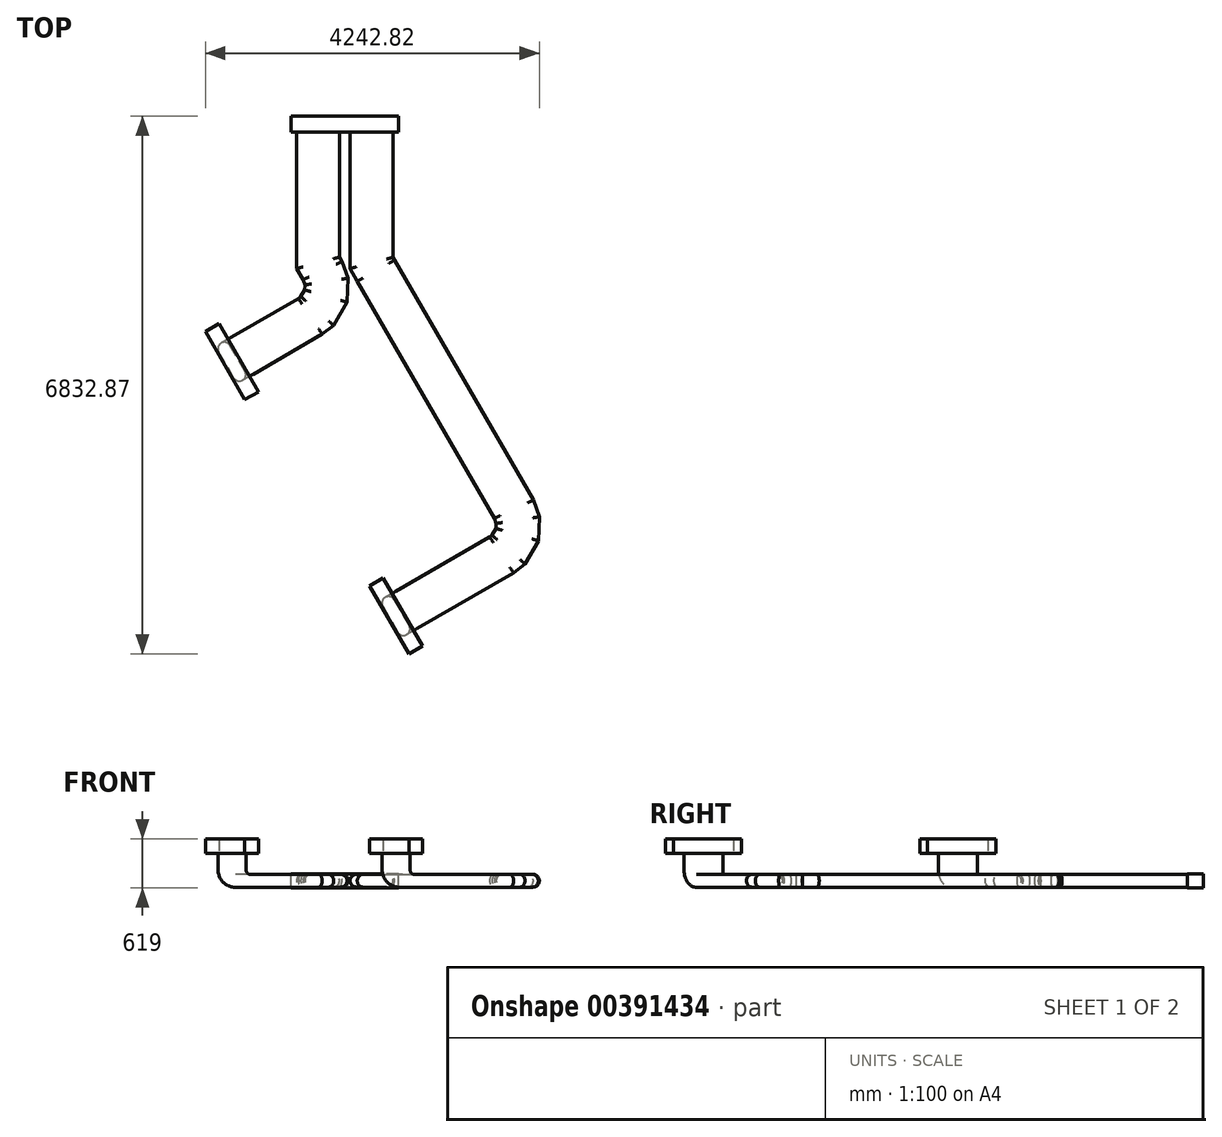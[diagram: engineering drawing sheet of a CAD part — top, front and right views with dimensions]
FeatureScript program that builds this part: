
annotation { "Feature Type Name" : "Feature", "Feature Type Description" : "" }
export const myFeature = defineFeature(function(context is Context, id is Id, definition is map)
    precondition{}
    {
        {
            var Q0;
            Q0=qCreatedBy(makeId("Front.planeOp"),FACE);
            var sketch = newSketch(context, id + "F0", { "sketchPlane" : qUnion([Q0])});
            skLineSegment(sketch, "E0.bottom", {"start": v(680, -89) * mm, "end": v(-680, -89) * mm});
            skLineSegment(sketch, "E0.top", {"start": v(680, 89) * mm, "end": v(-680, 89) * mm});
            skLineSegment(sketch, "E0.left", {"start": v(680, -89) * mm, "end": v(680, 89) * mm});
            skLineSegment(sketch, "E0.right", {"start": v(-680, -89) * mm, "end": v(-680, 89) * mm});
            skPoint(sketch, "E0.middle", {"position": v(0, 0) * mm});
            skSolve(sketch);
        }
        {
            var Q0;
            Q0=qSketchRegion(id+"F0",true);
            extrude(context, id + "F1", {"entities" : qUnion([Q0]), "depth" : 200 * mm});
        }
        {
            var Q0;
            Q0=makeQuery(id+"F1.opExtrude","CAP_FACE",FACE,{"disambiguationData":[OSD([sQuery(id+"F0.wireOp",EDGE,"E0.bottom"),sQuery(id+"F0.wireOp",EDGE,"E0.top"),sQuery(id+"F0.wireOp",EDGE,"E0.left"),sQuery(id+"F0.wireOp",EDGE,"E0.right")])],"isStart":false});
            var sketch = newSketch(context, id + "F2", { "sketchPlane" : qUnion([Q0])});
            skLineSegment(sketch, "E1.bottom", {"start": v(-150, -82.5) * mm, "end": v(-530, -82.5) * mm});
            skLineSegment(sketch, "E1.top", {"start": v(-150, 82.5) * mm, "end": v(-530, 82.5) * mm});
            skPoint(sketch, "E1.middle", {"position": v(-340, 0) * mm});
            skArc(sketch, "E2", {"start": v(-530, 82.5) * mm, "mid": v(-612.5, 0) * mm, "end": v(-530, -82.5) * mm});
            skArc(sketch, "E3", {"start": v(-150, -82.5) * mm, "mid": v(-67.5, 0) * mm, "end": v(-150, 82.5) * mm});
            skLineSegment(sketch, "E4.MirrorCS", {"start": v(150, -82.5) * mm, "end": v(530, -82.5) * mm});
            skLineSegment(sketch, "E5.MirrorCS", {"start": v(150, 82.5) * mm, "end": v(530, 82.5) * mm});
            skArc(sketch, "E6.MirrorCS", {"start": v(150, -82.5) * mm, "mid": v(67.5, 0) * mm, "end": v(150, 82.5) * mm});
            skArc(sketch, "E7.MirrorCS", {"start": v(530, 82.5) * mm, "mid": v(612.5, 0) * mm, "end": v(530, -82.5) * mm});
            skSolve(sketch);
        }
        {
            var Q0;
            Q0=makeQuery(id+"F2.imprint","IMPRINT",FACE,{"disambiguationData":[TD([[makeQuery(id+"F2.imprint","IMPRINT",EDGE,{"derivedFrom":sQuery(id+"F2.wireOp",EDGE,"E1.bottom")}),-1.0]])]});
            var Q1;
            Q1=makeQuery(id+"F2.imprint","IMPRINT",FACE,{"disambiguationData":[TD([[makeQuery(id+"F2.imprint","IMPRINT",EDGE,{"derivedFrom":sQuery(id+"F2.wireOp",EDGE,"E4.MirrorCS")}),1.0]])]});
            extrude(context, id + "F3", {"entities" : qUnion([Q0, Q1]), "operationType" : NewBodyOperationType.ADD, "depth" : 50 * mm});
        }
        {
            var Q0;
            Q0=makeQuery(id+"F1.opExtrude","SWEPT_BODY",BODY,{"disambiguationData":[OSD([sQuery(id+"F0.wireOp",EDGE,"E0.bottom"),sQuery(id+"F0.wireOp",EDGE,"E0.top"),sQuery(id+"F0.wireOp",EDGE,"E0.left"),sQuery(id+"F0.wireOp",EDGE,"E0.right")])]});
            transform(context, id + "F4", {"entities" : qUnion([Q0]), "transformType" : TransformType.TRANSLATION_3D, "dx" : 0 * mm, "dy" : 0 * mm, "dz" : 0 * mm, "makeCopy" : true});
        }
        {
            var Q0;
            Q0=makeQuery(id+"F4.opPattern","COPY",BODY,{"derivedFrom":makeQuery(id+"F1.opExtrude","SWEPT_BODY",BODY,{"disambiguationData":[OSD([sQuery(id+"F0.wireOp",EDGE,"E0.bottom"),sQuery(id+"F0.wireOp",EDGE,"E0.top"),sQuery(id+"F0.wireOp",EDGE,"E0.left"),sQuery(id+"F0.wireOp",EDGE,"E0.right")])]}),"instanceName":"1"});
            deleteBodies(context, id + "F5", {"entities" : qUnion([Q0])});
        }
        {
            var Q0;
            Q0=makeQuery(id+"F1.opExtrude","SWEPT_BODY",BODY,{"disambiguationData":[OSD([sQuery(id+"F0.wireOp",EDGE,"E0.bottom"),sQuery(id+"F0.wireOp",EDGE,"E0.top"),sQuery(id+"F0.wireOp",EDGE,"E0.left"),sQuery(id+"F0.wireOp",EDGE,"E0.right")])]});
            transform(context, id + "F6", {"entities" : qUnion([Q0]), "transformType" : TransformType.COPY});
        }
        {
            var Q0;
            Q0=makeQuery(id+"F6.opPattern","COPY",BODY,{"derivedFrom":makeQuery(id+"F1.opExtrude","SWEPT_BODY",BODY,{"disambiguationData":[OSD([sQuery(id+"F0.wireOp",EDGE,"E0.bottom"),sQuery(id+"F0.wireOp",EDGE,"E0.top"),sQuery(id+"F0.wireOp",EDGE,"E0.left"),sQuery(id+"F0.wireOp",EDGE,"E0.right")])]}),"instanceName":"1"});
            transform(context, id + "F7", {"entities" : qUnion([Q0]), "transformType" : TransformType.TRANSLATION_3D, "dx" : 0 * mm, "dy" : 0 * mm, "dz" : 0 * mm, "makeCopy" : true});
        }
        {
            var Q0;
            Q0=makeQuery(id+"F7.opPattern","COPY",BODY,{"derivedFrom":makeQuery(id+"F6.opPattern","COPY",BODY,{"derivedFrom":makeQuery(id+"F1.opExtrude","SWEPT_BODY",BODY,{"disambiguationData":[OSD([sQuery(id+"F0.wireOp",EDGE,"E0.bottom"),sQuery(id+"F0.wireOp",EDGE,"E0.top"),sQuery(id+"F0.wireOp",EDGE,"E0.left"),sQuery(id+"F0.wireOp",EDGE,"E0.right")])]}),"instanceName":"1"}),"instanceName":"1"});
            deleteBodies(context, id + "F8", {"entities" : qUnion([Q0])});
        }
        {
            var Q0;
            Q0=makeQuery(id+"F6.opPattern","COPY",BODY,{"derivedFrom":makeQuery(id+"F1.opExtrude","SWEPT_BODY",BODY,{"disambiguationData":[OSD([sQuery(id+"F0.wireOp",EDGE,"E0.bottom"),sQuery(id+"F0.wireOp",EDGE,"E0.top"),sQuery(id+"F0.wireOp",EDGE,"E0.left"),sQuery(id+"F0.wireOp",EDGE,"E0.right")])]}),"instanceName":"1"});
            deleteBodies(context, id + "F9", {"entities" : qUnion([Q0])});
        }
        {
            var Q0;
            Q0=makeQuery(id+"F3.opExtrude","CAP_FACE",FACE,{"disambiguationData":[OSD([sQuery(id+"F2.wireOp",EDGE,"E1.bottom"),sQuery(id+"F2.wireOp",EDGE,"E1.top"),sQuery(id+"F2.wireOp",EDGE,"E2"),sQuery(id+"F2.wireOp",EDGE,"E3")])],"isStart":false});
            var sketch = newSketch(context, id + "F10", { "sketchPlane" : qUnion([Q0])});
            skSolve(sketch);
        }
        {
            var Q0;
            Q0=makeQuery(id+"F10.imprint","IMPRINT",FACE,{"disambiguationData":[TD([[makeQuery(id+"F10.imprint","IMPRINT",EDGE,{"derivedFrom":makeQuery(id+"F3.opExtrude","CAP_EDGE",EDGE,{"disambiguationData":[OSD([sQuery(id+"F2.wireOp",EDGE,"E1.bottom")])],"isStart":false})}),-1.0]])]});
            var sketch = newSketch(context, id + "F11", { "sketchPlane" : qUnion([Q0])});
            skPoint(sketch, "E8.0", {"position": v(-340, 82.5) * mm});
            skPoint(sketch, "E8.1", {"position": v(-340, -82.5) * mm});
            skPoint(sketch, "E8.2", {"position": v(-612.5, 0) * mm});
            skPoint(sketch, "E8.3", {"position": v(-67.5, 0) * mm});
            skPoint(sketch, "E8.4", {"position": v(67.5, 0) * mm});
            skPoint(sketch, "E8.5", {"position": v(340, -82.5) * mm});
            skPoint(sketch, "E8.6", {"position": v(340, 82.5) * mm});
            skPoint(sketch, "E8.7", {"position": v(612.5, 0) * mm});
            skLineSegment(sketch, "E9", {"start": v(-612.5, 0) * mm, "end": v(612.5, 0) * mm, "construction": true});
            skLineSegment(sketch, "E10", {"start": v(-340, 82.5) * mm, "end": v(-340, -82.5) * mm, "construction": true});
            skLineSegment(sketch, "E11", {"start": v(340, 82.5) * mm, "end": v(340, -82.5) * mm, "construction": true});
            skPoint(sketch, "E12", {"position": v(-340, 0) * mm});
            skPoint(sketch, "E13", {"position": v(340, 0) * mm});
            skSolve(sketch);
        }
        {
            var Q0;
            Q0=qCreatedBy(makeId("Top.planeOp"),FACE);
            var sketch = newSketch(context, id + "F12", { "sketchPlane" : qUnion([Q0])});
            skPoint(sketch, "E14.0", {"position": v(340, -250) * mm});
            skPoint(sketch, "E14.1", {"position": v(-340, -250) * mm});
            skLineSegment(sketch, "E15", {"start": v(-340, -250) * mm, "end": v(-340, -1750) * mm});
            skLineSegment(sketch, "E16", {"start": v(340, -250) * mm, "end": v(340, -1750) * mm});
            skLineSegment(sketch, "E17", {"start": v(-283.06, -1962.5) * mm, "end": v(85, -1750) * mm, "construction": true});
            skLineSegment(sketch, "E18", {"start": v(395.32, -1963.44) * mm, "end": v(763.27, -1750.74) * mm, "construction": true});
            skLineSegment(sketch, "E19", {"start": v(-340, -1750) * mm, "end": v(85, -1750) * mm, "construction": true});
            skLineSegment(sketch, "E20", {"start": v(340, -1750) * mm, "end": v(765, -1750) * mm, "construction": true});
            skLineSegment(sketch, "E21", {"start": v(-340, -1750) * mm, "end": v(-340, -1864) * mm});
            skLineSegment(sketch, "E22", {"start": v(340, -1750) * mm, "end": v(340, -1864) * mm});
            skLineSegment(sketch, "E23", {"start": v(-340, -1864) * mm, "end": v(-283.06, -1962.5) * mm});
            skLineSegment(sketch, "E24", {"start": v(340, -1864) * mm, "end": v(395.32, -1963.44) * mm});
            skLineSegment(sketch, "E25", {"start": v(-283.06, -1962.5) * mm, "end": v(-651, -2175.2) * mm, "construction": true});
            skLineSegment(sketch, "E26", {"start": v(-651, -2175.2) * mm, "end": v(-232.5, -2101.17) * mm, "construction": true});
            skPoint(sketch, "E27", {"position": v(-438.31, -2543.14) * mm});
            skPoint(sketch, "E28", {"position": v(-350.33, -2475.56) * mm});
            skPoint(sketch, "E29", {"position": v(-240.43, -2284.98) * mm});
            skPoint(sketch, "E30", {"position": v(-232.5, -2101.17) * mm});
            skLineSegment(sketch, "E31", {"start": v(-283.06, -1962.5) * mm, "end": v(-232.5, -2101.17) * mm});
            skLineSegment(sketch, "E32", {"start": v(-232.5, -2101.17) * mm, "end": v(-240.43, -2284.98) * mm});
            skLineSegment(sketch, "E33", {"start": v(-240.43, -2284.98) * mm, "end": v(-350.33, -2475.56) * mm});
            skLineSegment(sketch, "E34", {"start": v(-350.33, -2475.56) * mm, "end": v(-438.31, -2543.14) * mm});
            skLineSegment(sketch, "E35", {"start": v(-438.31, -2543.14) * mm, "end": v(-651, -2175.2) * mm, "construction": true});
            skLineSegment(sketch, "E36", {"start": v(-438.31, -2543.14) * mm, "end": v(-1304.07, -3043.6) * mm});
            skLineSegment(sketch, "E37", {"start": v(395.32, -1963.44) * mm, "end": v(2146.94, -4993.59) * mm});
            skLineSegment(sketch, "E38", {"start": v(2146.94, -4993.59) * mm, "end": v(1779, -5206.29) * mm, "construction": true});
            skLineSegment(sketch, "E39", {"start": v(1779, -5206.29) * mm, "end": v(2197.5, -5132.26) * mm, "construction": true});
            skPoint(sketch, "E40", {"position": v(1991.69, -5574.23) * mm});
            skPoint(sketch, "E41", {"position": v(2079.67, -5506.64) * mm});
            skPoint(sketch, "E42", {"position": v(2189.57, -5316.06) * mm});
            skPoint(sketch, "E43", {"position": v(2197.5, -5132.26) * mm});
            skLineSegment(sketch, "E44", {"start": v(2146.94, -4993.59) * mm, "end": v(2197.5, -5132.26) * mm});
            skLineSegment(sketch, "E45", {"start": v(2197.5, -5132.26) * mm, "end": v(2189.57, -5316.06) * mm});
            skLineSegment(sketch, "E46", {"start": v(2189.57, -5316.06) * mm, "end": v(2079.67, -5506.64) * mm});
            skLineSegment(sketch, "E47", {"start": v(2079.67, -5506.64) * mm, "end": v(1991.69, -5574.23) * mm});
            skLineSegment(sketch, "E48", {"start": v(1779, -5206.29) * mm, "end": v(1991.69, -5574.23) * mm, "construction": true});
            skLineSegment(sketch, "E49", {"start": v(1991.69, -5574.23) * mm, "end": v(779.63, -6274.88) * mm});
            skSolve(sketch);
        }
        {
            var Q0;
            Q0=makeQuery(id+"F11.imprint","IMPRINT",FACE,{"disambiguationData":[TD([[makeQuery(id+"F11.imprint","IMPRINT",EDGE,{"derivedFrom":makeQuery(id+"F10.imprint","IMPRINT",EDGE,{"derivedFrom":makeQuery(id+"F3.opExtrude","CAP_EDGE",EDGE,{"disambiguationData":[OSD([sQuery(id+"F2.wireOp",EDGE,"E1.bottom")])],"isStart":false})})}),-1.0]])]});
            var Q1;
            Q1=sQuery(id+"F12.wireOp",EDGE,"E15");
            var Q2;
            Q2=sQuery(id+"F12.wireOp",EDGE,"E21");
            var Q3;
            Q3=sQuery(id+"F12.wireOp",EDGE,"E23");
            var Q4;
            Q4=sQuery(id+"F12.wireOp",EDGE,"E31");
            var Q5;
            Q5=sQuery(id+"F12.wireOp",EDGE,"E32");
            var Q6;
            Q6=sQuery(id+"F12.wireOp",EDGE,"E33");
            var Q7;
            Q7=sQuery(id+"F12.wireOp",EDGE,"E34");
            var Q8;
            Q8=sQuery(id+"F12.wireOp",EDGE,"E36");
            sweep(context, id + "F13", {"operationType" : NewBodyOperationType.ADD, "profiles" : qUnion([Q0]), "path" : qUnion([Q1, Q2, Q3, Q4, Q5, Q6, Q7, Q8])});
        }
        {
            var Q0;
            Q0=makeQuery(id+"F3.opExtrude","CAP_FACE",FACE,{"disambiguationData":[OSD([sQuery(id+"F2.wireOp",EDGE,"E4.MirrorCS"),sQuery(id+"F2.wireOp",EDGE,"E5.MirrorCS"),sQuery(id+"F2.wireOp",EDGE,"E6.MirrorCS"),sQuery(id+"F2.wireOp",EDGE,"E7.MirrorCS")])],"isStart":false});
            var Q1;
            Q1=sQuery(id+"F12.wireOp",EDGE,"E16");
            var Q2;
            Q2=sQuery(id+"F12.wireOp",EDGE,"E22");
            var Q3;
            Q3=sQuery(id+"F12.wireOp",EDGE,"E24");
            var Q4;
            Q4=sQuery(id+"F12.wireOp",EDGE,"E37");
            var Q5;
            Q5=sQuery(id+"F12.wireOp",EDGE,"E44");
            var Q6;
            Q6=sQuery(id+"F12.wireOp",EDGE,"E45");
            var Q7;
            Q7=sQuery(id+"F12.wireOp",EDGE,"E46");
            var Q8;
            Q8=sQuery(id+"F12.wireOp",EDGE,"E47");
            var Q9;
            Q9=sQuery(id+"F12.wireOp",EDGE,"E49");
            sweep(context, id + "F14", {"operationType" : NewBodyOperationType.ADD, "profiles" : qUnion([Q0]), "path" : qUnion([Q1, Q2, Q3, Q4, Q5, Q6, Q7, Q8, Q9])});
        }
        {
            var Q0;
            Q0=makeQuery(id+"F13.opSweep","CAP_FACE",FACE,{"disambiguationData":[OSD([sQuery(id+"F2.wireOp",EDGE,"E1.bottom"),sQuery(id+"F2.wireOp",EDGE,"E1.top"),sQuery(id+"F2.wireOp",EDGE,"E2"),sQuery(id+"F2.wireOp",EDGE,"E3"),sQuery(id+"F12.wireOp",VERTEX,"E36.end")])],"isStart":false});
            var sketch = newSketch(context, id + "F15", { "sketchPlane" : qUnion([Q0])});
            skLineSegment(sketch, "E50", {"start": v(2254.89, 0) * mm, "end": v(1709.89, 0) * mm, "construction": true});
            skLineSegment(sketch, "E51", {"start": v(1982.39, 82.5) * mm, "end": v(1982.39, -82.5) * mm, "construction": true});
            skSolve(sketch);
        }
        {
            var Q0;
            Q0=sQuery(id+"F15.wireOp",EDGE,"E50");
            cPlane(context, id + "F16", {"entities" : qUnion([Q0]), "cplaneType" : CPlaneType.LINE_ANGLE, "offset" : 25 * mm, "angle" : 0 * degree, "width" : 150 * mm, "height" : 150 * mm});
        }
        {
            var Q0;
            Q0=qCreatedBy(id+"F16.planeOp",FACE);
            var sketch = newSketch(context, id + "F17", { "sketchPlane" : qUnion([Q0])});
            skPoint(sketch, "E52.0", {"position": v(-1440.45, -2807.69) * mm});
            skPoint(sketch, "E52.1", {"position": v(-1167.7, -3279.53) * mm});
            skLineSegment(sketch, "E53", {"start": v(-1440.45, -2807.69) * mm, "end": v(-1440.45, -3341.26) * mm, "construction": true});
            skLineSegment(sketch, "E54", {"start": v(-1167.7, -3279.53) * mm, "end": v(-1440.45, -3279.53) * mm, "construction": true});
            skPoint(sketch, "E55.0", {"position": v(-1304.07, -3043.6) * mm});
            skLineSegment(sketch, "E56", {"start": v(-1304.07, -3043.6) * mm, "end": v(-1440.45, -3122.44) * mm, "construction": true});
            skLineSegment(sketch, "E57", {"start": v(-1304.07, -3043.6) * mm, "end": v(-1440.45, -3043.6) * mm, "construction": true});
            skSolve(sketch);
        }
        {
            var Q0;
            Q0=sQuery(id+"F17.wireOp",EDGE,"E56");
            cPlane(context, id + "F18", {"entities" : qUnion([Q0]), "cplaneType" : CPlaneType.LINE_ANGLE, "offset" : 25 * mm, "angle" : 0 * degree, "width" : 150 * mm, "height" : 150 * mm});
        }
        {
            var Q0;
            Q0=qCreatedBy(id+"F18.planeOp",FACE);
            var sketch = newSketch(context, id + "F19", { "sketchPlane" : qUnion([Q0])});
            skPoint(sketch, "E58.0", {"position": v(-2652.22, 0) * mm});
            skLineSegment(sketch, "E59", {"start": v(-2652.22, 0) * mm, "end": v(-2652.22, 150) * mm, "construction": true});
            skLineSegment(sketch, "E60", {"start": v(-2652.22, 150) * mm, "end": v(-2802.22, 150) * mm, "construction": true});
            skArc(sketch, "E61", {"start": v(-2802.22, 150) * mm, "mid": v(-2758.29, 43.93) * mm, "end": v(-2652.22, 0) * mm});
            skSolve(sketch);
        }
        {
            var Q0;
            {var subQ0=sQuery(id+"F12.wireOp",VERTEX,"E36.end");Q0=makeQuery(id+"F15.imprint","IMPRINT",FACE,{"disambiguationData":[TD([[makeQuery(id+"F15.imprint","IMPRINT",EDGE,{"derivedFrom":makeQuery(id+"F13.opSweep","CAP_EDGE",EDGE,{"disambiguationData":[OSD([sQuery(id+"F2.wireOp",EDGE,"E1.bottom"),subQ0])],"isStart":false})}),1.0]])]});}
            var Q1;
            Q1=sQuery(id+"F19.wireOp",EDGE,"E61");
            sweep(context, id + "F20", {"operationType" : NewBodyOperationType.ADD, "profiles" : qUnion([Q0]), "path" : qUnion([Q1])});
        }
        {
            var Q0;
            Q0=sQuery(id+"F12.wireOp",EDGE,"E49");
            cPlane(context, id + "F21", {"entities" : qUnion([Q0]), "cplaneType" : CPlaneType.LINE_ANGLE, "offset" : 25 * mm, "angle" : 0 * degree, "width" : 150 * mm, "height" : 150 * mm});
        }
        {
            var Q0;
            Q0=qCreatedBy(id+"F21.planeOp",FACE);
            var sketch = newSketch(context, id + "F22", { "sketchPlane" : qUnion([Q0])});
            skPoint(sketch, "E62.0", {"position": v(-2465.37, 0) * mm});
            skLineSegment(sketch, "E63", {"start": v(-2465.37, 0) * mm, "end": v(-2465.37, 150) * mm, "construction": true});
            skLineSegment(sketch, "E64", {"start": v(-2465.37, 150) * mm, "end": v(-2615.37, 150) * mm, "construction": true});
            skArc(sketch, "E65", {"start": v(-2465.37, 0) * mm, "mid": v(-2571.44, 43.93) * mm, "end": v(-2615.37, 150) * mm});
            skSolve(sketch);
        }
        {
            var Q0;
            Q0=makeQuery(id+"F14.opSweep","CAP_FACE",FACE,{"disambiguationData":[OSD([sQuery(id+"F2.wireOp",EDGE,"E4.MirrorCS"),sQuery(id+"F2.wireOp",EDGE,"E5.MirrorCS"),sQuery(id+"F2.wireOp",EDGE,"E6.MirrorCS"),sQuery(id+"F2.wireOp",EDGE,"E7.MirrorCS"),sQuery(id+"F12.wireOp",VERTEX,"E49.end")])],"isStart":false});
            var Q1;
            Q1=sQuery(id+"F22.wireOp",EDGE,"E65");
            sweep(context, id + "F23", {"operationType" : NewBodyOperationType.ADD, "profiles" : qUnion([Q0]), "path" : qUnion([Q1])});
        }
        {
            var Q0;
            Q0=makeQuery(id+"F20.opSweep","CAP_FACE",FACE,{"disambiguationData":[OSD([sQuery(id+"F2.wireOp",EDGE,"E1.bottom"),sQuery(id+"F2.wireOp",EDGE,"E1.top"),sQuery(id+"F2.wireOp",EDGE,"E2"),sQuery(id+"F2.wireOp",EDGE,"E3"),sQuery(id+"F12.wireOp",VERTEX,"E36.end"),sQuery(id+"F19.wireOp",VERTEX,"E61.start")])],"isStart":false});
            extrude(context, id + "F24", {"entities" : qUnion([Q0]), "operationType" : NewBodyOperationType.ADD, "depth" : 200 * mm});
        }
        {
            var Q0;
            Q0=makeQuery(id+"F23.opSweep","CAP_FACE",FACE,{"disambiguationData":[OSD([sQuery(id+"F2.wireOp",EDGE,"E4.MirrorCS"),sQuery(id+"F2.wireOp",EDGE,"E5.MirrorCS"),sQuery(id+"F2.wireOp",EDGE,"E6.MirrorCS"),sQuery(id+"F2.wireOp",EDGE,"E7.MirrorCS"),sQuery(id+"F12.wireOp",VERTEX,"E49.end"),sQuery(id+"F22.wireOp",VERTEX,"E65.end")])],"isStart":false});
            extrude(context, id + "F25", {"entities" : qUnion([Q0]), "operationType" : NewBodyOperationType.ADD, "depth" : 200 * mm});
        }
        {
            var Q0;
            Q0=makeQuery(id+"F24.opExtrude","CAP_FACE",FACE,{"disambiguationData":[OSD([sQuery(id+"F2.wireOp",EDGE,"E1.bottom"),sQuery(id+"F2.wireOp",EDGE,"E1.top"),sQuery(id+"F2.wireOp",EDGE,"E2"),sQuery(id+"F2.wireOp",EDGE,"E3"),sQuery(id+"F12.wireOp",VERTEX,"E36.end"),sQuery(id+"F19.wireOp",VERTEX,"E61.start")])],"isStart":false});
            var sketch = newSketch(context, id + "F26", { "sketchPlane" : qUnion([Q0])});
            skLineSegment(sketch, "E66", {"start": v(-1505.36, -3159.96) * mm, "end": v(-1362.5, -3077.39) * mm, "construction": true});
            skPoint(sketch, "E67", {"position": v(-1433.93, -3118.68) * mm});
            skLineSegment(sketch, "E68", {"start": v(-1433.93, -3118.68) * mm, "end": v(-1520.5, -3168.72) * mm, "construction": true});
            skLineSegment(sketch, "E69", {"start": v(-1520.5, -3168.72) * mm, "end": v(-1770.74, -2735.84) * mm});
            skLineSegment(sketch, "E70", {"start": v(-1770.74, -2735.84) * mm, "end": v(-1597.59, -2635.75) * mm});
            skLineSegment(sketch, "E71", {"start": v(-1597.59, -2635.75) * mm, "end": v(-1097.13, -3501.5) * mm});
            skLineSegment(sketch, "E72", {"start": v(-1097.13, -3501.5) * mm, "end": v(-1270.28, -3601.6) * mm});
            skLineSegment(sketch, "E73", {"start": v(-1270.28, -3601.6) * mm, "end": v(-1520.5, -3168.72) * mm});
            skSolve(sketch);
        }
        {
            var Q0;
            Q0=makeQuery(id+"F26.imprint","IMPRINT",FACE,{"disambiguationData":[TD([[makeQuery(id+"F26.imprint","IMPRINT",EDGE,{"derivedFrom":sQuery(id+"F26.wireOp",EDGE,"E69")}),-1.0]])]});
            var Q1;
            {var subQ0=sQuery(id+"F19.wireOp",VERTEX,"E61.start");var subQ1=sQuery(id+"F12.wireOp",VERTEX,"E36.end");Q1=makeQuery(id+"F26.imprint","IMPRINT",FACE,{"disambiguationData":[TD([[makeQuery(id+"F26.imprint","IMPRINT",EDGE,{"derivedFrom":makeQuery(id+"F24.opExtrude","CAP_EDGE",EDGE,{"disambiguationData":[OSD([sQuery(id+"F2.wireOp",EDGE,"E1.bottom"),subQ1,subQ0])],"isStart":false})}),1.0]])]});}
            extrude(context, id + "F27", {"entities" : qUnion([Q0, Q1]), "operationType" : NewBodyOperationType.ADD, "depth" : 180 * mm});
        }
        {
            var Q0;
            Q0=makeQuery(id+"F25.opExtrude","CAP_FACE",FACE,{"disambiguationData":[OSD([sQuery(id+"F2.wireOp",EDGE,"E4.MirrorCS"),sQuery(id+"F2.wireOp",EDGE,"E5.MirrorCS"),sQuery(id+"F2.wireOp",EDGE,"E6.MirrorCS"),sQuery(id+"F2.wireOp",EDGE,"E7.MirrorCS"),sQuery(id+"F12.wireOp",VERTEX,"E49.end"),sQuery(id+"F22.wireOp",VERTEX,"E65.end")])],"isStart":false});
            var sketch = newSketch(context, id + "F28", { "sketchPlane" : qUnion([Q0])});
            skLineSegment(sketch, "E74", {"start": v(721.19, -6308.66) * mm, "end": v(578.34, -6391.24) * mm, "construction": true});
            skPoint(sketch, "E75", {"position": v(649.76, -6349.95) * mm});
            skLineSegment(sketch, "E76", {"start": v(649.76, -6349.95) * mm, "end": v(563.19, -6400) * mm, "construction": true});
            skLineSegment(sketch, "E77", {"start": v(563.19, -6400) * mm, "end": v(813.42, -6832.87) * mm});
            skLineSegment(sketch, "E78", {"start": v(563.19, -6400) * mm, "end": v(312.96, -5967.12) * mm});
            skLineSegment(sketch, "E79", {"start": v(312.96, -5967.12) * mm, "end": v(486.1, -5867.02) * mm});
            skLineSegment(sketch, "E80", {"start": v(486.1, -5867.02) * mm, "end": v(986.57, -6732.78) * mm});
            skLineSegment(sketch, "E81", {"start": v(986.57, -6732.78) * mm, "end": v(813.42, -6832.87) * mm});
            skSolve(sketch);
        }
        {
            var Q0;
            Q0=makeQuery(id+"F28.imprint","IMPRINT",FACE,{"disambiguationData":[TD([[makeQuery(id+"F28.imprint","IMPRINT",EDGE,{"derivedFrom":sQuery(id+"F28.wireOp",EDGE,"E77")}),1.0]])]});
            var Q1;
            {var subQ0=sQuery(id+"F22.wireOp",VERTEX,"E65.end");var subQ1=sQuery(id+"F12.wireOp",VERTEX,"E49.end");Q1=makeQuery(id+"F28.imprint","IMPRINT",FACE,{"disambiguationData":[TD([[makeQuery(id+"F28.imprint","IMPRINT",EDGE,{"derivedFrom":makeQuery(id+"F25.opExtrude","CAP_EDGE",EDGE,{"disambiguationData":[OSD([sQuery(id+"F2.wireOp",EDGE,"E4.MirrorCS"),subQ1,subQ0])],"isStart":false})}),1.0]])]});}
            extrude(context, id + "F29", {"entities" : qUnion([Q0, Q1]), "operationType" : NewBodyOperationType.ADD, "depth" : 180 * mm});
        }
    });
